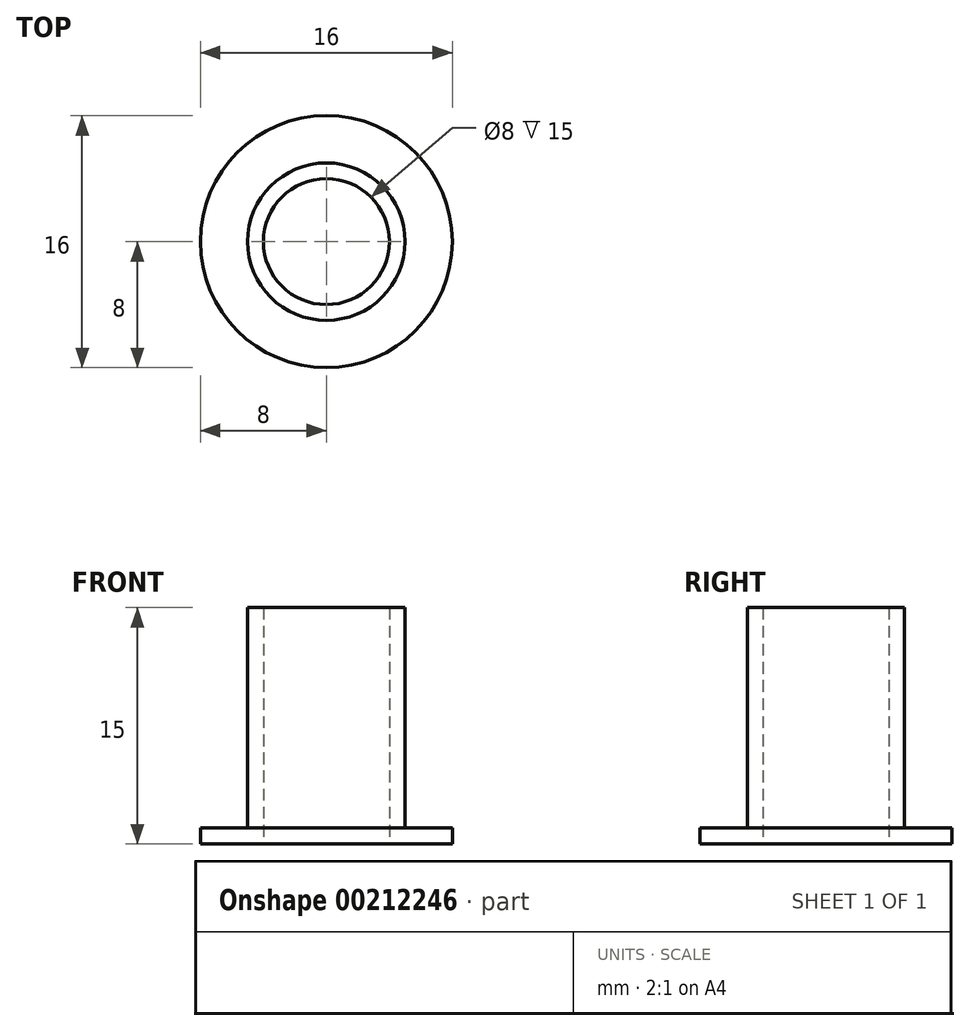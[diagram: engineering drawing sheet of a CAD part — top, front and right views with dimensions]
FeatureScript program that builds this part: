
annotation { "Feature Type Name" : "Feature", "Feature Type Description" : "" }
export const myFeature = defineFeature(function(context is Context, id is Id, definition is map)
    precondition{}
    {
        {
            var Q0;
            Q0=qCreatedBy(makeId("Front.planeOp"),FACE);
            var sketch = newSketch(context, id + "F0", { "sketchPlane" : qUnion([Q0])});
            skLineSegment(sketch, "E0", {"start": v(-4, 0) * mm, "end": v(-8, 0) * mm});
            skLineSegment(sketch, "E1", {"start": v(-8, 0) * mm, "end": v(-8, 1) * mm});
            skLineSegment(sketch, "E2", {"start": v(-8, 1) * mm, "end": v(-5, 1) * mm});
            skLineSegment(sketch, "E3", {"start": v(-5, 1) * mm, "end": v(-5, 15) * mm});
            skLineSegment(sketch, "E4", {"start": v(-5, 15) * mm, "end": v(-4, 15) * mm});
            skLineSegment(sketch, "E5", {"start": v(-4, 15) * mm, "end": v(-4, 0) * mm});
            skLineSegment(sketch, "E6", {"start": v(0, 0) * mm, "end": v(0, 15) * mm, "construction": true});
            skSolve(sketch);
        }
        {
            var Q0;
            Q0=makeQuery(id+"F0.imprint","IMPRINT",FACE,{"disambiguationData":[TD([[makeQuery(id+"F0.imprint","IMPRINT",EDGE,{"derivedFrom":sQuery(id+"F0.wireOp",EDGE,"E0")}),-1.0]])]});
            var Q1;
            Q1=sQuery(id+"F0.wireOp",EDGE,"E6");
            revolve(context, id + "F1", {"entities" : qUnion([Q0]), "axis" : qUnion([Q1]), "revolveType" : RevolveType.FULL});
        }
    });
